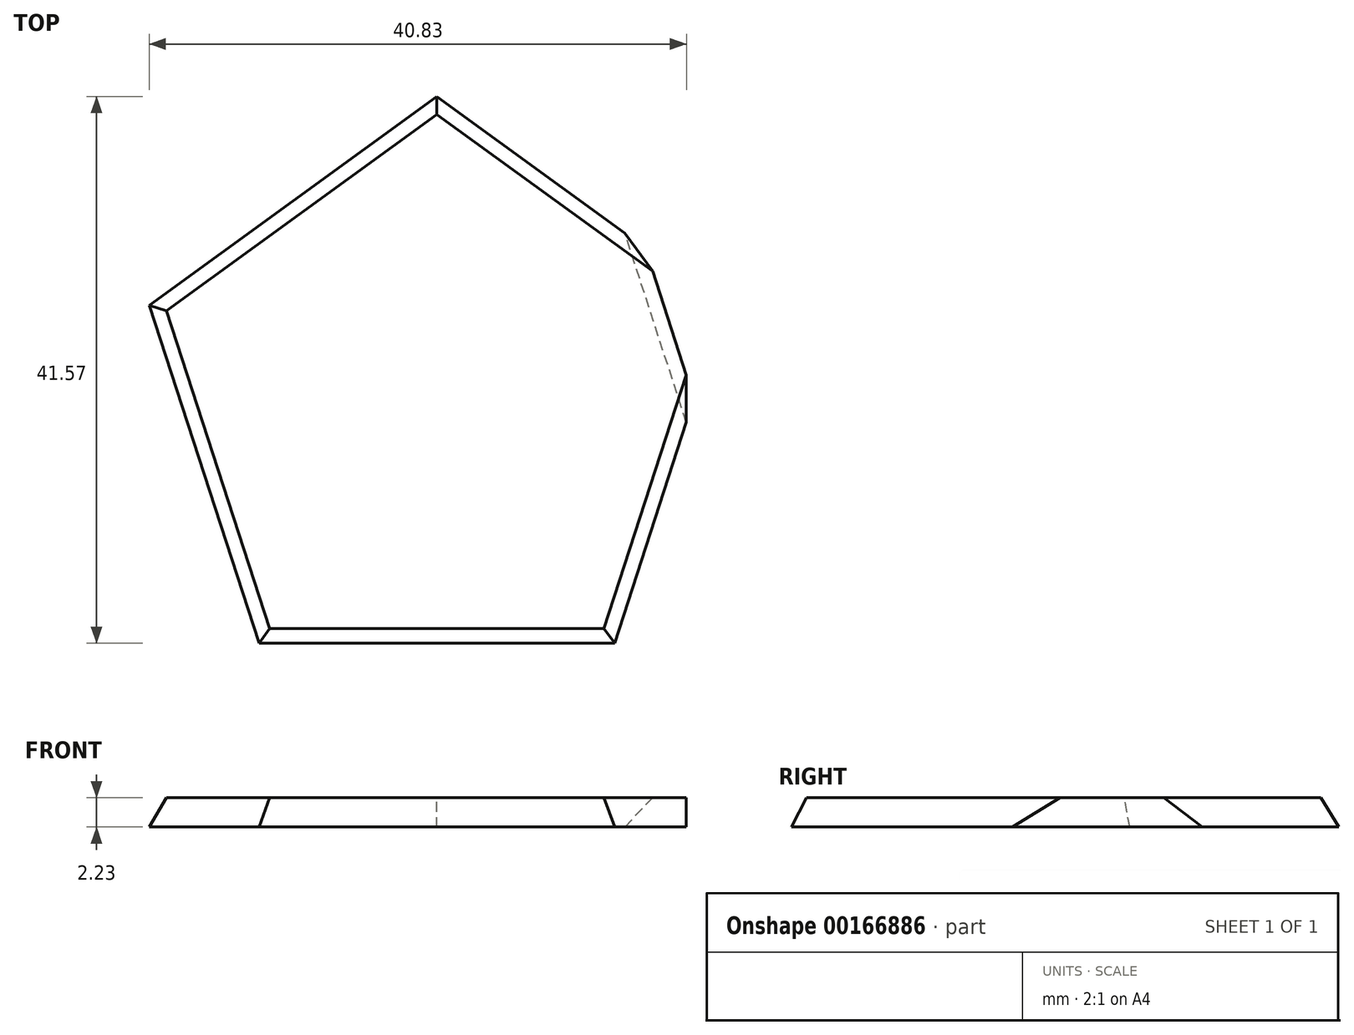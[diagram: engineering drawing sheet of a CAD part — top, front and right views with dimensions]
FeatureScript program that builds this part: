
annotation { "Feature Type Name" : "Feature", "Feature Type Description" : "" }
export const myFeature = defineFeature(function(context is Context, id is Id, definition is map)
    precondition{}
    {
        {
            var Q0;
            Q0=qCreatedBy(makeId("Top.planeOp"),FACE);
            var sketch = newSketch(context, id + "F0", { "sketchPlane" : qUnion([Q0])});
            skCircle(sketch, "E0.cCircle", {"center": v(0, 0) * mm, "radius": 17.48 * mm, "construction": true});
            skLineSegment(sketch, "E0.0", {"start": v(0, 21.6) * mm, "end": v(20.55, 6.68) * mm});
            skLineSegment(sketch, "E0.1", {"start": v(20.55, 6.68) * mm, "end": v(12.7, -17.48) * mm});
            skLineSegment(sketch, "E0.2", {"start": v(12.7, -17.48) * mm, "end": v(-12.7, -17.48) * mm});
            skLineSegment(sketch, "E0.3", {"start": v(-12.7, -17.48) * mm, "end": v(-20.55, 6.68) * mm});
            skLineSegment(sketch, "E0.4", {"start": v(-20.55, 6.68) * mm, "end": v(0, 21.6) * mm});
            skPoint(sketch, "E0.0.midPoint", {"position": v(10.27, 14.14) * mm});
            skSolve(sketch);
        }
        {
            var Q0;
            Q0=makeQuery(id+"F0.imprint","IMPRINT",FACE,{"disambiguationData":[TD([[makeQuery(id+"F0.imprint","IMPRINT",EDGE,{"derivedFrom":sQuery(id+"F0.wireOp",EDGE,"E0.0")}),-1.0]])]});
            extrude(context, id + "F1", {"entities" : qUnion([Q0]), "oppositeDirection" : true, "depth" : ((1 / sin(36 * degree)) * (sin(18 * degree) + 1)) * mm, "hasDraft" : true, "draftAngle" : acos(-1 / sqrt(5)) - 90 * degree});
        }
        {
            var Q0;
            Q0=makeQuery(id+"F1.opExtrude","CAP_FACE",FACE,{"disambiguationData":[OSD([sQuery(id+"F0.wireOp",EDGE,"E0.0"),sQuery(id+"F0.wireOp",EDGE,"E0.1"),sQuery(id+"F0.wireOp",EDGE,"E0.2"),sQuery(id+"F0.wireOp",EDGE,"E0.3"),sQuery(id+"F0.wireOp",EDGE,"E0.4")])],"isStart":false});
            var sketch = newSketch(context, id + "F2", { "sketchPlane" : qUnion([Q0])});
            skCircle(sketch, "E1.cCircle", {"center": v(0, 0) * mm, "radius": 17.48 * mm, "construction": true});
            skLineSegment(sketch, "E1.0", {"start": v(20.55, 6.68) * mm, "end": v(12.7, -17.48) * mm});
            skLineSegment(sketch, "E1.1", {"start": v(12.7, -17.48) * mm, "end": v(-12.7, -17.48) * mm});
            skLineSegment(sketch, "E1.2", {"start": v(-12.7, -17.48) * mm, "end": v(-20.55, 6.68) * mm});
            skLineSegment(sketch, "E1.3", {"start": v(-20.55, 6.68) * mm, "end": v(0, 21.6) * mm});
            skLineSegment(sketch, "E1.4", {"start": v(0, 21.6) * mm, "end": v(20.55, 6.68) * mm});
            skPoint(sketch, "E1.0.midPoint", {"position": v(16.62, -5.4) * mm});
            skSolve(sketch);
        }
        {
            var Q0;
            Q0=makeQuery(id+"F2.imprint","IMPRINT",FACE,{"disambiguationData":[TD([[makeQuery(id+"F2.imprint","IMPRINT",EDGE,{"derivedFrom":sQuery(id+"F2.wireOp",EDGE,"E1.0")}),1.0]])]});
            extrude(context, id + "F3", {"entities" : qUnion([Q0]), "operationType" : NewBodyOperationType.REMOVE, "endBound" : BoundingType.THROUGH_ALL, "oppositeDirection" : true, "depth" : 34.04 * mm, "hasDraft" : true, "draftAngle" : acos(-1 / sqrt(5)) - 90 * degree, "draftPullDirection" : true});
        }
    });
